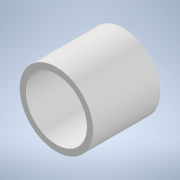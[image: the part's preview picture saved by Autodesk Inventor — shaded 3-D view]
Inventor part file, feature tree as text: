
AUTODESK INVENTOR PART (.ipt)
format: ipt  version: 2021 (Build 250183000, 183)  size: 161,280 bytes
history: native  units: mm
features: other x4, extrude x3, fillet x3, sketch x3, pattern_circular x1, reference x1, projected_geometry x1
ambient origin geometry x8: Origin, YZ Plane, XZ Plane, XY Plane, X Axis, Y Axis, Z Axis, Center Point
bodies: Body1 (feature_tree)
feature tree (16):
  other  "Bryła1"
  extrude  "Wyciągnięcie proste1"  Depth=12.0mm
  extrude  "Wyciągnięcie proste2"  Depth=1.0mm TaperAngle=0.0deg
  fillet  "Zaokrąglenie1"  Radius=1.0mm
  extrude  "Wyciągnięcie proste3"  Depth=10.0mm TaperAngle=0.0deg
  fillet  "Zaokrąglenie2"  Radius=25.0mm
  fillet  "Zaokrąglenie3"  Radius=20.0mm
  pattern_circular  "Szyk kołowy1"  [2 undecoded]
  sketch  "Szkic1"
  reference  "Odniesienie1"
  sketch  "Szkic2"
  sketch  "Szkic3"
  projected_geometry  "Pętla rzutowana1"
  parser-record x1  (decoder bookkeeping rows leaked as tree rows — omitted from the tree; the rows remain in map.json)
  other  "zespoluchwyt.iam"
  other  "uchwyt1:1"
note: 2 required parameter values undecoded (feature->parameter linkage not recoverable at this tier; creation-order binding heuristic only, values carry confidence <= 0.55)
note: 1 file-system path scrubbed to <path> (originals preserved in map.json)
